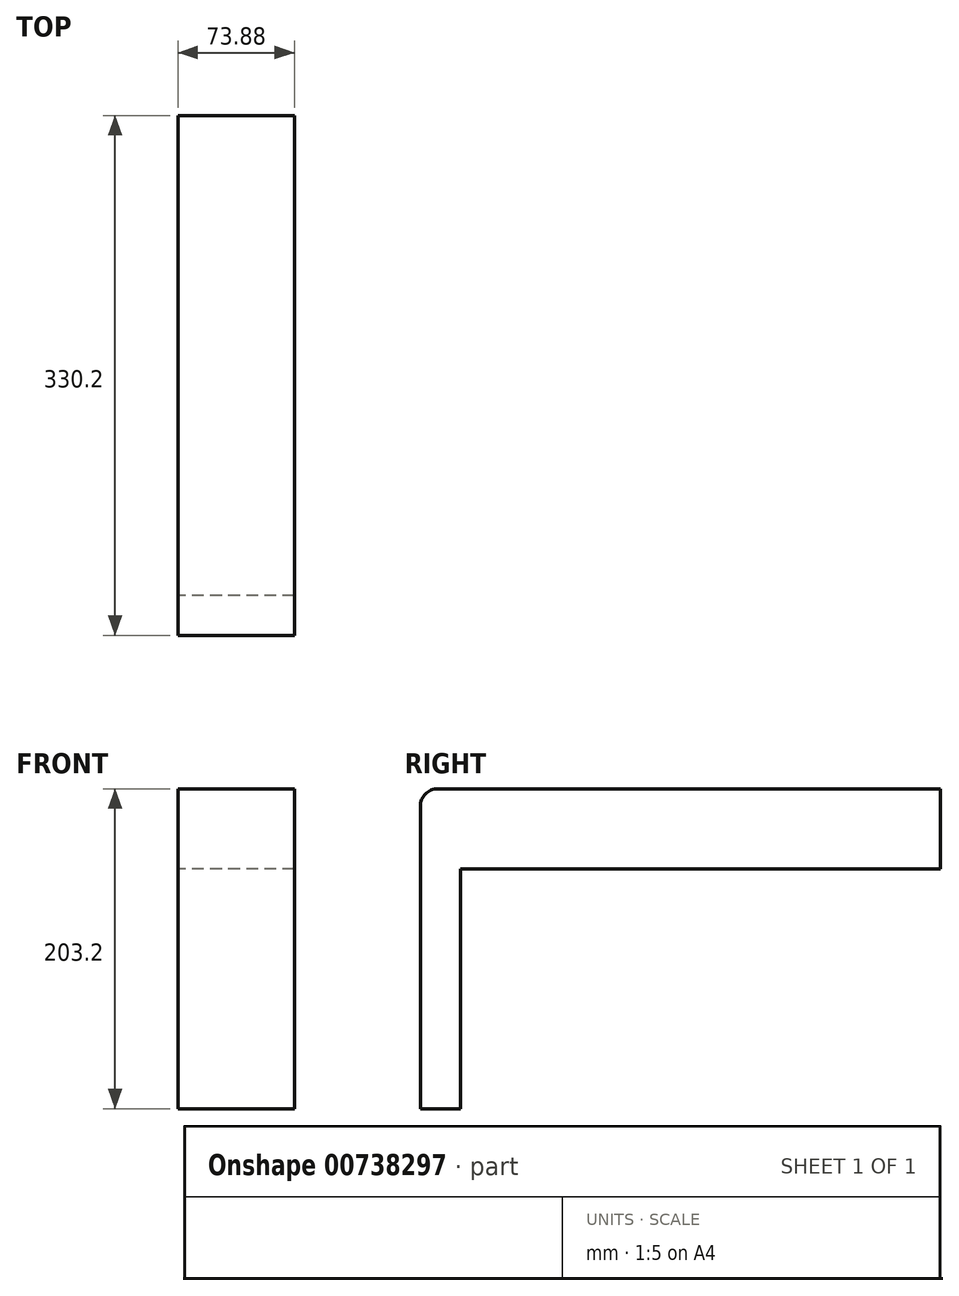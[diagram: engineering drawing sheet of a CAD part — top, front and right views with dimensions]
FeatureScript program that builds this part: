
annotation { "Feature Type Name" : "Feature", "Feature Type Description" : "" }
export const myFeature = defineFeature(function(context is Context, id is Id, definition is map)
    precondition{}
    {
        {
            var Q0;
            Q0=qCreatedBy(makeId("Right.planeOp"),FACE);
            var sketch = newSketch(context, id + "F0", { "sketchPlane" : qUnion([Q0])});
            skLineSegment(sketch, "E0", {"start": v(-304.8, 0) * mm, "end": v(-304.8, 152.4) * mm});
            skLineSegment(sketch, "E1", {"start": v(-304.8, 152.4) * mm, "end": v(0, 152.4) * mm});
            skLineSegment(sketch, "E2", {"start": v(0, 152.4) * mm, "end": v(0, 203.2) * mm});
            skLineSegment(sketch, "E3", {"start": v(-304.8, 0) * mm, "end": v(-330.2, 0) * mm});
            skLineSegment(sketch, "E4", {"start": v(0, 203.2) * mm, "end": v(-319.09, 203.2) * mm});
            skLineSegment(sketch, "E5", {"start": v(-330.2, 192.09) * mm, "end": v(-330.2, 0) * mm});
            skPoint(sketch, "E6.visualSharp", {"position": v(-330.2, 203.2) * mm});
            skArc(sketch, "E6.filletArc", {"start": v(-319.09, 203.2) * mm, "mid": v(-326.95, 199.95) * mm, "end": v(-330.2, 192.09) * mm});
            skSolve(sketch);
        }
        {
            var Q0;
            Q0=makeQuery(id+"F0.imprint","IMPRINT",FACE,{"disambiguationData":[TD([[makeQuery(id+"F0.imprint","IMPRINT",EDGE,{"derivedFrom":sQuery(id+"F0.wireOp",EDGE,"E0")}),1.0]])]});
            extrude(context, id + "F1", {"entities" : qUnion([Q0]), "depth" : (73 + (7 / 8)) * mm, "offsetDistance" : 25.4 * mm});
        }
    });
